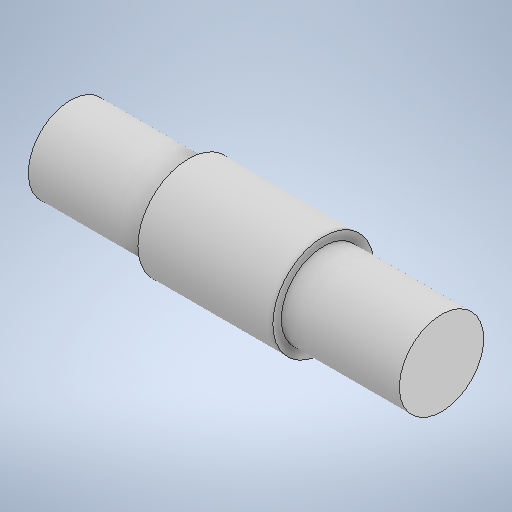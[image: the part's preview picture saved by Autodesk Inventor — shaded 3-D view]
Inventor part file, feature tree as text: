
AUTODESK INVENTOR PART (.ipt)
format: ipt  version: 2025.1 (Build 291241000, 241)  size: 248,832 bytes
history: native  units: mm
features: revolve x1, sketch x1
ambient origin geometry x8: Origin, YZ Plane, XZ Plane, XY Plane, X Axis, Y Axis, Z Axis, Center Point
bodies: Solid1 (feature_tree)
feature tree (2):
  revolve  "Revolution1"  [1 undecoded]
  sketch  "Sketch1"  dims[d0=5.0mm d1=6.0mm d2=7.0mm d3=7.0mm d4=8.0mm d5=90.0deg]
note: 1 required parameter value undecoded (feature->parameter linkage not recoverable at this tier; creation-order binding heuristic only, values carry confidence <= 0.55)
